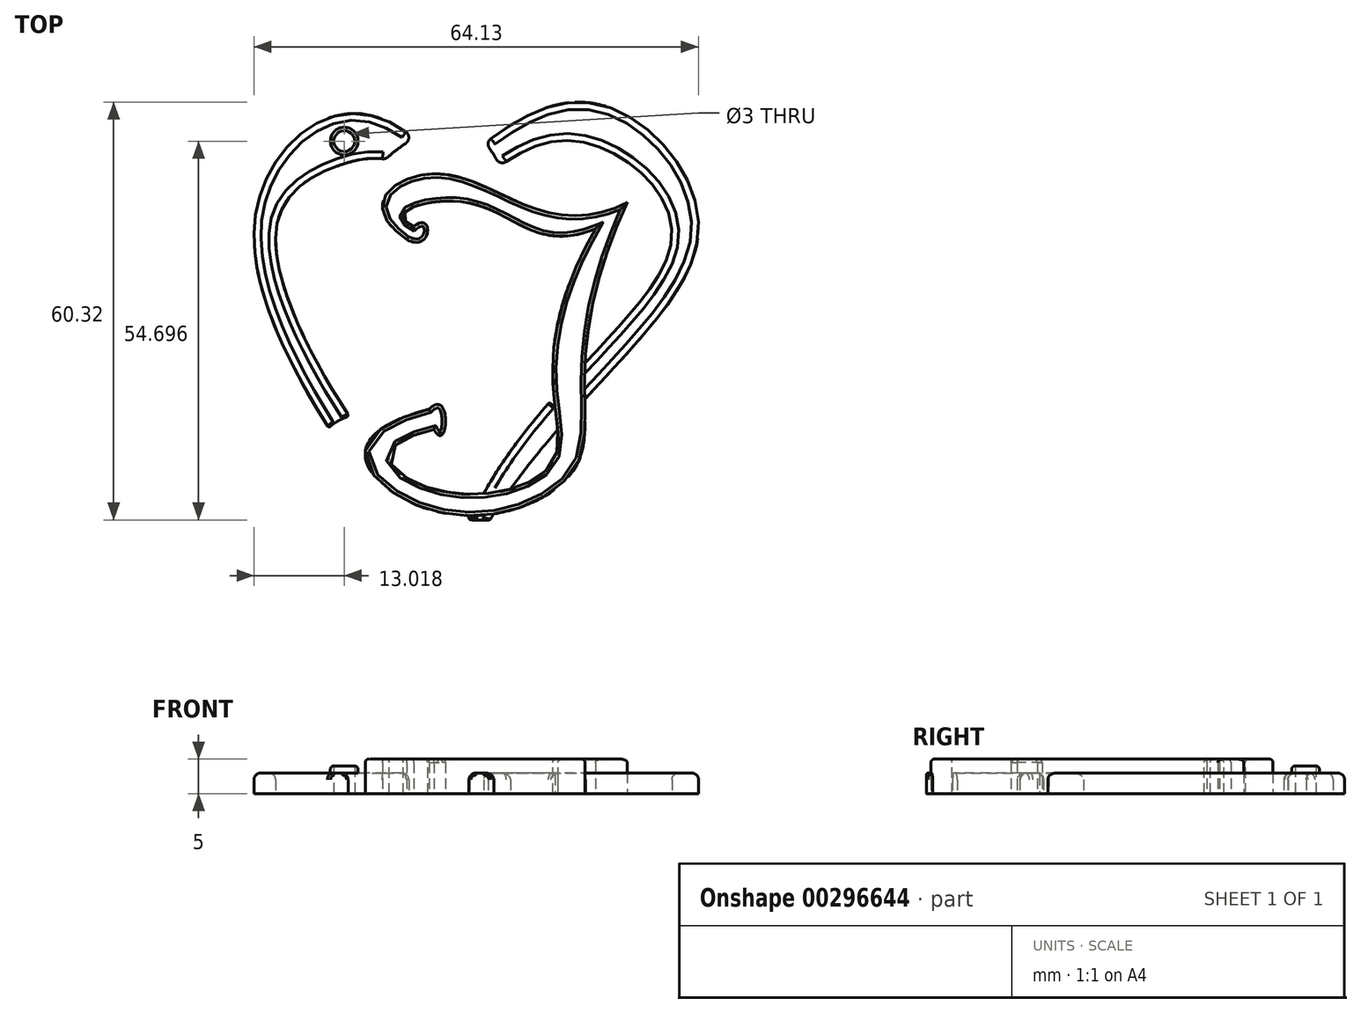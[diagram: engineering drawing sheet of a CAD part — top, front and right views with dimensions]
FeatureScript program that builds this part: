
annotation { "Feature Type Name" : "Feature", "Feature Type Description" : "" }
export const myFeature = defineFeature(function(context is Context, id is Id, definition is map)
    precondition{}
    {
        {
            var Q0;
            Q0=qCreatedBy(makeId("Top.planeOp"),FACE);
            var sketch = newSketch(context, id + "F0", { "sketchPlane" : qUnion([Q0])});
            skFitSpline(sketch, "E0", {"points": [v(-34.86, 46.59) * mm, v(-28.17, 50.24) * mm, v(-8.65, 46.3) * mm], "startDerivative": vector(-34.78, 18) * mm, "endDerivative": vector(44.55, 17.55) * mm});
            skFitSpline(sketch, "E1", {"points": [v(-8.65, 46.3) * mm, v(-14.8, 12.63) * mm, v(-33.27, 9.14) * mm, v(-31.94, 17.35) * mm], "startDerivative": vector(-75.86, -134.2) * mm, "endDerivative": vector(141.17, 34.22) * mm});
            skFitSpline(sketch, "E2", {"points": [v(-35.87, 44.74) * mm, v(-32.15, 54.24) * mm, v(-4.05, 50.08) * mm], "startDerivative": vector(-59.18, 41.17) * mm, "endDerivative": vector(58.99, 29.22) * mm});
            skFitSpline(sketch, "E3", {"points": [v(-4.05, 50.08) * mm, v(-11.73, 11.59) * mm, v(-34.2, 6.36) * mm, v(-32.65, 20.26) * mm], "startDerivative": vector(-74.16, -161.08) * mm, "endDerivative": vector(179.51, 45.86) * mm});
            skFitSpline(sketch, "E4", {"points": [v(-35.87, 44.74) * mm, v(-34.86, 46.59) * mm], "startDerivative": vector(11.58, -5.93) * mm, "endDerivative": vector(-8.54, -7.59) * mm});
            skFitSpline(sketch, "E5", {"points": [v(-32.65, 20.26) * mm, v(-31.94, 17.35) * mm], "startDerivative": vector(10.04, 10.04) * mm, "endDerivative": vector(-6.29, 11.58) * mm});
            skSolve(sketch);
        }
        {
            var Q0;
            Q0=qCreatedBy(makeId("Top.planeOp"),FACE);
            var sketch = newSketch(context, id + "F1", { "sketchPlane" : qUnion([Q0])});
            skFitSpline(sketch, "E6.0", {"points": [v(-35.87, 44.74) * mm, v(-43.27, 49.89) * mm, v(-27.61, 60.95) * mm, v(-16.35, 44) * mm, v(-4.05, 50.08) * mm]});
            skFitSpline(sketch, "E7.0", {"points": [v(-4.05, 50.08) * mm, v(-14.5, 27.37) * mm, v(-1.93, 11.3) * mm, v(-32.96, -0.13) * mm, v(-47.76, 16.4) * mm, v(-32.65, 20.26) * mm]});
            skFitSpline(sketch, "E8", {"points": [v(-29.98, 54.12) * mm, v(-44.88, 62.87) * mm, v(-57.8, 47.51) * mm, v(-29.42, -7.03) * mm], "startDerivative": vector(-46.86, 65.9) * mm, "endDerivative": vector(97.47, -125.32) * mm});
            skFitSpline(sketch, "E9", {"points": [v(-29.98, 54.12) * mm, v(-7.04, 63.95) * mm, v(6.12, 44.91) * mm, v(-29.42, -7.03) * mm], "startDerivative": vector(92.73, 83.65) * mm, "endDerivative": vector(-61.88, -166.74) * mm});
            skFitSpline(sketch, "E10", {"points": [v(-35.05, 53.74) * mm, v(-45.66, 55.45) * mm, v(-54.56, 47.08) * mm, v(-41.5, 15.29) * mm], "startDerivative": vector(-27.16, 41.36) * mm, "endDerivative": vector(51.76, -73.8) * mm});
            skFitSpline(sketch, "E11", {"points": [v(-36.04, 7.2) * mm, v(-29.95, -1.68) * mm], "startDerivative": vector(6.3, -10.56) * mm, "endDerivative": vector(5.4, -8.82) * mm});
            skFitSpline(sketch, "E12", {"points": [v(-29.95, -1.68) * mm, v(-26.74, 4.92) * mm], "startDerivative": vector(4.13, 8.46) * mm, "endDerivative": vector(5.08, 8.8) * mm});
            skFitSpline(sketch, "E13.0", {"points": [v(-8.65, 46.3) * mm, v(-19.96, 26.27) * mm, v(-5.34, 11.73) * mm, v(-31.81, 5) * mm, v(-42.33, 14.84) * mm, v(-31.94, 17.35) * mm]});
            skFitSpline(sketch, "E14", {"points": [v(-24.77, 8.05) * mm, v(2.4, 45.22) * mm, v(-8.96, 58.45) * mm, v(-25.57, 52.8) * mm], "startDerivative": vector(61.31, 112.03) * mm, "endDerivative": vector(-65.87, -58.5) * mm});
            skFitSpline(sketch, "E15", {"points": [v(-26.74, 4.92) * mm, v(-24.77, 8.05) * mm], "startDerivative": vector(1.97, 3.13) * mm, "endDerivative": vector(1.97, 3.13) * mm});
            skCircle(sketch, "E16", {"center": v(-44.88, 58.97) * mm, "radius": 1.5 * mm});
            skSolve(sketch);
        }
        {
            var Q0;
            Q0=makeQuery(id+"F0.imprint","IMPRINT",FACE,{"disambiguationData":[TD([[makeQuery(id+"F0.imprint","IMPRINT",EDGE,{"derivedFrom":sQuery(id+"F0.wireOp",EDGE,"E0")}),1.0]])]});
            extrude(context, id + "F2", {"entities" : qUnion([Q0]), "depth" : 5 * mm});
        }
        {
            var Q0;
            {var subQ0=sQuery(id+"F1.wireOp",EDGE,"E8");Q0=makeQuery(id+"F1.imprint","IMPRINT",FACE,{"disambiguationData":[TD([[makeQuery(id+"F1.imprint","IMPRINT",EDGE,{"derivedFrom":subQ0}),1.0]])]});}
            var Q1;
            {var subQ0=sQuery(id+"F1.wireOp",EDGE,"E13.0");var subQ1=sQuery(id+"F1.wireOp",EDGE,"E9");var subQ2=makeQuery(id+"F1.imprint","INTERSECT",VERTEX,{"disambiguationData":[OD(0.0)],"derivedFrom":[subQ1,subQ0]});Q1=makeQuery(id+"F1.imprint","IMPRINT",FACE,{"disambiguationData":[TD([[makeQuery(id+"F1.imprint","IMPRINT",EDGE,{"disambiguationData":[TD([[subQ2,-1.0]])],"derivedFrom":subQ1}),-1.0]])]});}
            var Q2;
            {var subQ0=sQuery(id+"F1.wireOp",EDGE,"E9");var subQ5=sQuery(id+"F1.wireOp",EDGE,"E7.0");var subQ6=makeQuery(id+"F1.imprint","INTERSECT",VERTEX,{"disambiguationData":[OD(0.0)],"derivedFrom":[subQ5,subQ0]});Q2=makeQuery(id+"F1.imprint","IMPRINT",FACE,{"disambiguationData":[TD([[makeQuery(id+"F1.imprint","IMPRINT",EDGE,{"disambiguationData":[TD([[subQ6,1.0]])],"derivedFrom":subQ5}),1.0]])]});}
            extrude(context, id + "F3", {"entities" : qUnion([Q0, Q1, Q2]), "operationType" : NewBodyOperationType.ADD, "depth" : 3 * mm});
        }
        {
            var Q0;
            Q0=makeQuery(id+"F3.opExtrude","CAP_EDGE",EDGE,{"disambiguationData":[OSD([sQuery(id+"F1.wireOp",EDGE,"E8")])],"isStart":false});
            var Q1;
            Q1=makeQuery(id+"F3.opExtrude","CAP_EDGE",EDGE,{"disambiguationData":[OSD([sQuery(id+"F1.wireOp",EDGE,"E10")])],"isStart":false});
            var Q2;
            Q2=makeQuery(id+"F3.opExtrude","CAP_EDGE",EDGE,{"disambiguationData":[OSD([sQuery(id+"F1.wireOp",EDGE,"E11")])],"isStart":false});
            var Q3;
            Q3=makeQuery(id+"F3.opExtrude","CAP_EDGE",EDGE,{"disambiguationData":[OSD([sQuery(id+"F1.wireOp",EDGE,"E12")])],"isStart":false});
            var Q4;
            {var subQ0=sQuery(id+"F1.wireOp",EDGE,"E9");Q4=makeQuery(id+"F3.opExtrude","CAP_EDGE",EDGE,{"disambiguationData":[OSD([subQ0]),TDD([makeQuery(id+"F1.imprint","IMPRINT",EDGE,{"disambiguationData":[TD([[makeQuery(id+"F1.imprint","INTERSECT",VERTEX,{"derivedFrom":[sQuery(id+"F1.wireOp",EDGE,"E8"),subQ0]}),1.0]])],"derivedFrom":subQ0})])],"isStart":false});}
            var Q5;
            {var subQ0=sQuery(id+"F1.wireOp",EDGE,"E14");var subQ1=sQuery(id+"F1.wireOp",EDGE,"E13.0");Q5=makeQuery(id+"F3.opExtrude","CAP_EDGE",EDGE,{"disambiguationData":[OSD([subQ0]),TDD([makeQuery(id+"F1.imprint","IMPRINT",EDGE,{"disambiguationData":[TD([[makeQuery(id+"F1.imprint","INTERSECT",VERTEX,{"derivedFrom":[subQ1,subQ0]}),1.0]])],"derivedFrom":subQ0})])],"isStart":false});}
            var Q6;
            {var subQ0=sQuery(id+"F1.wireOp",EDGE,"E13.0");var subQ1=sQuery(id+"F1.wireOp",EDGE,"E9");Q6=makeQuery(id+"F3.opExtrude","CAP_EDGE",EDGE,{"disambiguationData":[OSD([subQ1]),TDD([makeQuery(id+"F1.imprint","IMPRINT",EDGE,{"disambiguationData":[TD([[makeQuery(id+"F1.imprint","INTERSECT",VERTEX,{"disambiguationData":[OD(0.0)],"derivedFrom":[subQ1,subQ0]}),-1.0]])],"derivedFrom":subQ1})])],"isStart":false});}
            var Q7;
            {var subQ0=sQuery(id+"F1.wireOp",EDGE,"E14");Q7=makeQuery(id+"F3.opExtrude","CAP_EDGE",EDGE,{"disambiguationData":[OSD([subQ0]),TDD([makeQuery(id+"F1.imprint","IMPRINT",EDGE,{"disambiguationData":[TD([[makeQuery(id+"F1.imprint","INTERSECT",VERTEX,{"derivedFrom":[sQuery(id+"F1.wireOp",EDGE,"E6.0"),subQ0]}),1.0]])],"derivedFrom":subQ0})])],"isStart":false});}
            fillet(context, id + "F4", {"entities" : qUnion([Q0, Q1, Q2, Q3, Q4, Q5, Q6, Q7]), "radius" : 1 * mm, "tangentPropagation" : true, "allowEdgeOverflow" : false});
        }
        {
            var Q0;
            {var subQ0=sQuery(id+"F1.wireOp",EDGE,"E9");Q0=makeQuery(id+"F3.opExtrude","CAP_EDGE",EDGE,{"disambiguationData":[OSD([subQ0]),TDD([makeQuery(id+"F1.imprint","IMPRINT",EDGE,{"disambiguationData":[TD([[makeQuery(id+"F1.imprint","INTERSECT",VERTEX,{"disambiguationData":[OD(0.0)],"derivedFrom":[sQuery(id+"F1.wireOp",EDGE,"E7.0"),subQ0]}),1.0]])],"derivedFrom":subQ0})])],"isStart":false});}
            fillet(context, id + "F5", {"entities" : qUnion([Q0]), "radius" : 1 * mm, "tangentPropagation" : true, "allowEdgeOverflow" : false});
        }
        {
            var Q0;
            {var subQ0=sQuery(id+"F1.wireOp",EDGE,"E6.0");Q0=makeQuery(id+"F3.opExtrude","CAP_EDGE",EDGE,{"disambiguationData":[OSD([subQ0]),TDD([makeQuery(id+"F1.imprint","IMPRINT",EDGE,{"disambiguationData":[TD([[makeQuery(id+"F1.imprint","INTERSECT",VERTEX,{"derivedFrom":[subQ0,sQuery(id+"F1.wireOp",EDGE,"E10")]}),-1.0]])],"derivedFrom":subQ0})])],"isStart":false});}
            var Q1;
            {var subQ0=sQuery(id+"F1.wireOp",EDGE,"E6.0");Q1=makeQuery(id+"F3.opExtrude","CAP_EDGE",EDGE,{"disambiguationData":[OSD([subQ0]),TDD([makeQuery(id+"F1.imprint","IMPRINT",EDGE,{"disambiguationData":[TD([[makeQuery(id+"F1.imprint","INTERSECT",VERTEX,{"derivedFrom":[subQ0,sQuery(id+"F1.wireOp",EDGE,"E14")]}),1.0]])],"derivedFrom":subQ0})])],"isStart":false});}
            fillet(context, id + "F6", {"entities" : qUnion([Q0, Q1]), "radius" : 1 * mm, "tangentPropagation" : true, "allowEdgeOverflow" : false});
        }
        {
            var Q0;
            Q0=makeQuery(id+"F3.opExtrude","CAP_FACE",FACE,{"disambiguationData":[OSD([sQuery(id+"F1.wireOp",EDGE,"E6.0"),sQuery(id+"F1.wireOp",EDGE,"E7.0"),sQuery(id+"F1.wireOp",EDGE,"E8"),sQuery(id+"F1.wireOp",EDGE,"E9"),sQuery(id+"F1.wireOp",EDGE,"E10"),sQuery(id+"F1.wireOp",EDGE,"E11"),sQuery(id+"F1.wireOp",EDGE,"E12"),sQuery(id+"F1.wireOp",EDGE,"E16")])],"isStart":false});
            var sketch = newSketch(context, id + "F7", { "sketchPlane" : qUnion([Q0])});
            skCircle(sketch, "E17.0", {"center": v(-44.88, 58.97) * mm, "radius": 1.5 * mm});
            skCircle(sketch, "E18", {"center": v(-44.88, 58.97) * mm, "radius": 2 * mm});
            skSolve(sketch);
        }
        {
            var Q0;
            Q0=makeQuery(id+"F7.imprint","IMPRINT",FACE,{"disambiguationData":[TD([[makeQuery(id+"F7.imprint","IMPRINT",EDGE,{"derivedFrom":sQuery(id+"F7.wireOp",EDGE,"E17.0")}),-1.0]])]});
            extrude(context, id + "F8", {"entities" : qUnion([Q0]), "operationType" : NewBodyOperationType.ADD, "depth" : 1 * mm});
        }
        {
            var Q0;
            Q0=makeQuery(id+"F8.opExtrude","CAP_EDGE",EDGE,{"disambiguationData":[OSD([sQuery(id+"F7.wireOp",EDGE,"E18")])],"isStart":false});
            fillet(context, id + "F9", {"entities" : qUnion([Q0]), "radius" : 0.5 * mm, "tangentPropagation" : true, "allowEdgeOverflow" : false});
        }
        {
            var Q0;
            Q0=makeQuery(id+"F9.opFillet","BLEND_EDGE",EDGE,{"blendedFrom":[makeQuery(id+"F8.opExtrude","CAP_EDGE",EDGE,{"disambiguationData":[OSD([sQuery(id+"F7.wireOp",EDGE,"E18")])],"isStart":false}),makeQuery(id+"F8.boolean.opBoolean","MERGE",FACE,{"derivedFrom":[makeQuery(id+"F3.opExtrude","SWEPT_FACE",FACE,{"disambiguationData":[OSD([sQuery(id+"F1.wireOp",EDGE,"E16")])]}),makeQuery(id+"F8.opExtrude","SWEPT_FACE",FACE,{"disambiguationData":[OSD([sQuery(id+"F7.wireOp",EDGE,"E17.0")])]})]})],"blendedInto":[makeQuery(id+"F8.boolean.opBoolean","MERGE",FACE,{"derivedFrom":[makeQuery(id+"F3.opExtrude","SWEPT_FACE",FACE,{"disambiguationData":[OSD([sQuery(id+"F1.wireOp",EDGE,"E16")])]}),makeQuery(id+"F8.opExtrude","SWEPT_FACE",FACE,{"disambiguationData":[OSD([sQuery(id+"F7.wireOp",EDGE,"E17.0")])]})]})]});
            fillet(context, id + "F10", {"entities" : qUnion([Q0]), "radius" : 0.1 * mm, "tangentPropagation" : true, "rho" : 0.5, "crossSection" : FilletCrossSection.CONIC, "allowEdgeOverflow" : false});
        }
        {
            var Q0;
            {var subQ0=sQuery(id+"F1.wireOp",EDGE,"E13.0");Q0=makeQuery(id+"F3.opExtrude","CAP_EDGE",EDGE,{"disambiguationData":[OSD([subQ0]),TDD([makeQuery(id+"F1.imprint","IMPRINT",EDGE,{"disambiguationData":[TD([[makeQuery(id+"F1.imprint","INTERSECT",VERTEX,{"derivedFrom":[subQ0,sQuery(id+"F1.wireOp",EDGE,"E14")]}),-1.0]])],"derivedFrom":subQ0})])],"isStart":false});}
            var Q1;
            {var subQ0=sQuery(id+"F1.wireOp",EDGE,"E7.0");Q1=makeQuery(id+"F3.opExtrude","CAP_EDGE",EDGE,{"disambiguationData":[OSD([subQ0]),TDD([makeQuery(id+"F1.imprint","IMPRINT",EDGE,{"disambiguationData":[TD([[makeQuery(id+"F1.imprint","INTERSECT",VERTEX,{"disambiguationData":[OD(1.0)],"derivedFrom":[subQ0,sQuery(id+"F1.wireOp",EDGE,"E9")]}),-1.0]])],"derivedFrom":subQ0})])],"isStart":false});}
            var Q2;
            {var subQ0=sQuery(id+"F1.wireOp",EDGE,"E7.0");Q2=makeQuery(id+"F3.opExtrude","CAP_EDGE",EDGE,{"disambiguationData":[OSD([subQ0]),TDD([makeQuery(id+"F1.imprint","IMPRINT",EDGE,{"disambiguationData":[TD([[makeQuery(id+"F1.imprint","INTERSECT",VERTEX,{"derivedFrom":[subQ0,sQuery(id+"F1.wireOp",EDGE,"E10")]}),1.0]])],"derivedFrom":subQ0})])],"isStart":false});}
            var Q3;
            {var subQ0=sQuery(id+"F1.wireOp",EDGE,"E7.0");Q3=makeQuery(id+"F3.opExtrude","CAP_EDGE",EDGE,{"disambiguationData":[OSD([subQ0]),TDD([makeQuery(id+"F1.imprint","IMPRINT",EDGE,{"disambiguationData":[TD([[makeQuery(id+"F1.imprint","INTERSECT",VERTEX,{"disambiguationData":[OD(0.0)],"derivedFrom":[subQ0,sQuery(id+"F1.wireOp",EDGE,"E9")]}),1.0]])],"derivedFrom":subQ0})])],"isStart":false});}
            var Q4;
            {var subQ0=sQuery(id+"F1.wireOp",EDGE,"E13.0");Q4=makeQuery(id+"F3.opExtrude","CAP_EDGE",EDGE,{"disambiguationData":[OSD([subQ0]),TDD([makeQuery(id+"F1.imprint","IMPRINT",EDGE,{"disambiguationData":[TD([[makeQuery(id+"F1.imprint","INTERSECT",VERTEX,{"disambiguationData":[OD(1.0)],"derivedFrom":[sQuery(id+"F1.wireOp",EDGE,"E9"),subQ0]}),-1.0]])],"derivedFrom":subQ0})])],"isStart":false});}
            fillet(context, id + "F11", {"entities" : qUnion([Q0, Q1, Q2, Q3, Q4]), "radius" : 0.3 * mm, "tangentPropagation" : true, "allowEdgeOverflow" : false});
        }
        {
            var Q0;
            Q0=makeQuery(id+"F2.opExtrude","CAP_FACE",FACE,{"disambiguationData":[OSD([sQuery(id+"F0.wireOp",EDGE,"E0"),sQuery(id+"F0.wireOp",EDGE,"E1"),sQuery(id+"F0.wireOp",EDGE,"E2"),sQuery(id+"F0.wireOp",EDGE,"E3"),sQuery(id+"F0.wireOp",EDGE,"E4"),sQuery(id+"F0.wireOp",EDGE,"E5")])],"isStart":false});
            fillet(context, id + "F12", {"entities" : qUnion([Q0]), "radius" : 0.5 * mm, "tangentPropagation" : true, "allowEdgeOverflow" : false});
        }
    });
